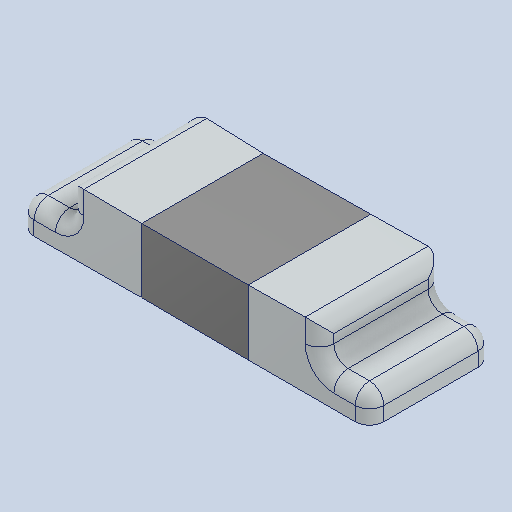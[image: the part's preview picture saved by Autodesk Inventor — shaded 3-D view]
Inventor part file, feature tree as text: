
AUTODESK INVENTOR PART (.ipt)
format: ipt  version: 2024 (Build 280153000, 153)  size: 141,824 bytes
history: native  units: in
note: dims shown in document units (in); Inventor stores cm internally (conversion verified against a paired STEP export)
features: mirror x1
ambient origin geometry x8: Origin, YZ Plane, XZ Plane, XY Plane, X Axis, Y Axis, Z Axis, Center Point
bodies: Solid1 (feature_tree)
feature tree (1):
  mirror  "Mirror1"
